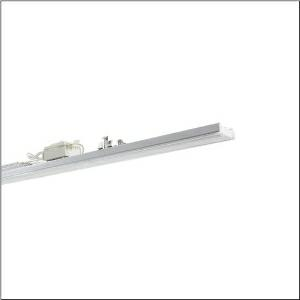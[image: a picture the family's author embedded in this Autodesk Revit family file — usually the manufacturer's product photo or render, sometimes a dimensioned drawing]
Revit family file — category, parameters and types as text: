
# Revit family: licross_r__21_recessed_mo_52tl11cn49xg_87da
name_source: partatom
category: Lighting Fixtures
units: mm (PartAtom-declared; Revit-internal decimal feet)

## family parameters
Cut with Voids When Loaded = No
Host = Face
Light Source = No
Part Type = Normal
Room Calculation Point = No
Round Connector Dimension = Use Diameter
Shared = No

## types (1)
- --- (1 x LED, 9120 lm, 49.9 W, 4000K)
    Apparent Load = 50 VA
    CIE Flux Codes = 89 96 99 100 100
    Color Rendering = 80
    Color Temperature = 4000K
    Default Elevation = 1800 mm
    Description = Licross® 21 Recessed MO, luminaire insert, of sheet steel, galvanised, coil coated, white, length: 1.500mm, width: 66mm, height: 67mm, LED rated luminous flux: 9.120lm, light colour: 840, control gear: ON/OFF Multilumen, CLOi, control gear: ECG Multilumen, with plug, 3-pole, with phase selection, mains connection: 220..240V, AC, 50/60Hz, start of lifetime: 50W, end of service life: 61W, halogen-free wiring, primary light control with lens, of plastic, primary optical cover: cover, of PMMA, light emission: direct distribution, primary light characteristic: symmetric, protection rating (complete): IP40, insulation class (complete): insulation class I (protective earthing), certification: CE, ENEC, VDE, UKCA, protection symbol: D if used in an environment without relevant dust loads with corresponding accessories, impact resistance: IK06, permissible ambient temperature for indoor applications: -35..+40°C, corresponds to IFS (International Featured Standards) requirements for safety and quality in the food industry, reducing of maximum allowable ambient temperature of 5°C with ceiling mounting, LABS conformity tested according to VDMA 24364:2018-05, packaging unit: 1 piece
    Height = 58 mm
    Lamp = 1 x LED
    Lamp Light Flux = 9120 lm
    Lamp Power = 49.9 W
    Lamp count = 1
    Length = 1500 mm
    Luminous efficacy = 183 lm/W
    Manufacturer = Siteco
    ModVariant = No
    Model = 52TL11CN49XG
    Mounting Place = Ceiling
    Mounting Type = Pendant
    Number of Poles = 1
    OnlyDefault = Yes
    Power Factor = 1
    Product Name = Licross® 21 Recessed MO
    Product group = luminaire insert
    ProductGroupID = 902
    Protection Class = Protection class I
    Protection Degree = IP 40
    RLX_Detail_Level = 1
    RLX_Emergency_Light_Flux = 0 lm
    RLX_Emergency_Type = 0
    RLX_Emergency_Type_DB = No
    RlxData = <blob elided: 22245 chars, md5=27250995>
    Socket = socket
    Standby Power = 0 W
    System Light Flux = 9120 lm
    System Power = 50 W
    Type Comments = factory setting: luminous flux: 100 % | (A | C | E) | 116 mA
    Type Image = l_1296930.jpg
    URL = http://relux.com
    VarID = @adj_110686
    Voltage = 0 V
    Weight = 0.00 kg
    Width = 66 mm

## geometry (parser evidence)
native form markers: Blend x4, Sweep x12
no freeform markers — native parametric forms only
